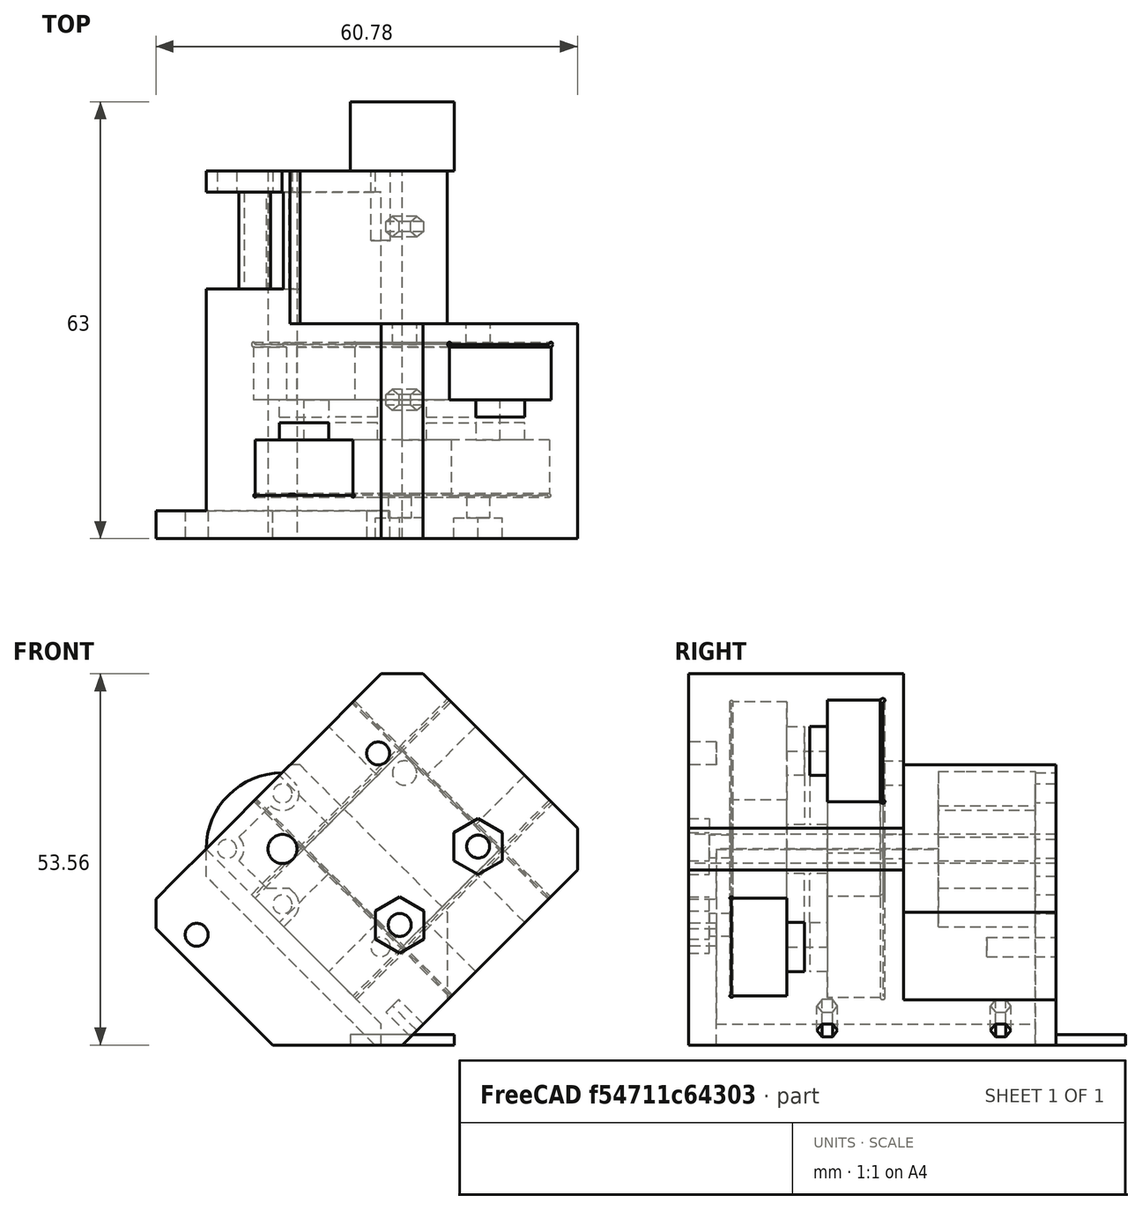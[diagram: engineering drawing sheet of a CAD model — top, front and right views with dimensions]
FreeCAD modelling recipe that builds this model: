
FCSTD DOCUMENT  (FreeCAD 0.19R)
Label: ToolHead_ScreenClearance
License: All rights reserved
LicenseURL: http://en.wikipedia.org/wiki/All_rights_reserved
objects: Sketcher::SketchObject×20, PartDesign::Pocket×14, PartDesign::Pad×4, PartDesign::Chamfer×2, PartDesign::Body×1, Mesh::Feature×1
note: 61 computed .brp shape members not serialized (recipe doc carries the construction recipe); baked Part::Feature solids carry a one-line shape summary decoded from their .brp

FEATURE [Sketcher::SketchObject] Sketch  label="Body001"
  FullyConstrained = true
  MapMode = 5
  Support = -> [XY_Plane]
  sketch-geometry (11):
    g0: LineSegment StartX=20 StartY=15.7574 StartZ=0 EndX=20 EndY=-15.7574 EndZ=0
    g1: LineSegment StartX=15.7574 StartY=-20 StartZ=0 EndX=-20 EndY=-20 EndZ=0
    g2: LineSegment StartX=-20 StartY=-15.7574 StartZ=0 EndX=-20 EndY=19.9515 EndZ=0
    g3: Circle CenterX=-12.1976 CenterY=12.1976 CenterZ=0 NormalX=0 NormalY=0 NormalZ=1 AngleXU=0 Radius=2.1
    g4: LineSegment StartX=-12.1976 StartY=12.1976 StartZ=0 EndX=0 EndY=0 EndZ=0
    g5: ArcOfCircle CenterX=-12.1976 CenterY=12.1976 CenterZ=0 NormalX=0 NormalY=0 NormalZ=1 AngleXU=0 Radius=11 StartAngle=0.788519 EndAngle=2.35931
    g6: LineSegment StartX=-4.44373 StartY=20 StartZ=0 EndX=15.7574 EndY=20 EndZ=0
    g7: LineSegment StartX=15.7574 StartY=-20 StartZ=0 EndX=20 EndY=-15.7574 EndZ=0
    g8: LineSegment StartX=-20 StartY=-15.7574 StartZ=0 EndX=-22.1213 EndY=-17.8787 EndZ=0
    g9: LineSegment StartX=-22.1213 StartY=-17.8787 StartZ=0 EndX=-20 EndY=-20 EndZ=0
    g10: LineSegment StartX=15.7574 StartY=20 StartZ=0 EndX=20 EndY=15.7574 EndZ=0
  constraints (32):
    c: Horizontal(g1)
    c: Vertical(g0)
    c: Vertical(g2)
    c: Distance(g-1,g3) = 17.25
    c: Coincident(g4,g3)
    c: Coincident(g4,g-1)
    c: Angle(g4) = -0.785398
    c: Diameter(g3) = 4.2
    c: Coincident(g5,g3)
    c: Diameter(g5) = 22
    c: DistanceX(g1) = -20
    c: Coincident(g6,g5)
    c: Horizontal(g6)
    c: Coincident(g5,g2)
    c: Coincident(g7,g1)
    c: Coincident(g7,g0)
    c: Angle(g7) = 0.785398
    c: Distance(g7) = 6
    c: DistanceY(g1) = -20
    c: Coincident(g2,g8)
    c: Coincident(g8,g9)
    c: Coincident(g9,g1)
    c: Angle(g9) = -0.785398
    c: Angle(g8) = -2.35619
    c: Distance(g9) = 3
    c: DistanceX(g2) = -20
    c: Coincident(g10,g6)
    c: Coincident(g10,g0)
    c: Distance(g10) = 6
    c: Angle(g10) = -0.785398
    c: DistanceX(g0) = 20
    c: DistanceY(g6) = 20
FEATURE [PartDesign::Pad] Pad
  Direction = (1,1,1)
  Length = 53
  Length2 = 10
  Profile = -> Sketch
  Reversed = true
  Type = 0
FEATURE [Sketcher::SketchObject] Sketch001  label="RailHole"
  FullyConstrained = true
  MapMode = 5
  Placement = pos=(20,0,0) rot=(0.57735,0.57735,0.57735;2.0944rad)
  Support = -> [Pad]
  sketch-geometry (10):
    g0: LineSegment StartX=-10.35 StartY=-27.65 StartZ=0 EndX=-10.35 EndY=-20 EndZ=0
    g1: LineSegment StartX=5 StartY=-17.5 StartZ=0 EndX=-5 EndY=-17.5 EndZ=0
    g2: LineSegment StartX=10 StartY=-28 StartZ=0 EndX=-10 EndY=-28 EndZ=0
    g3: LineSegment StartX=5 StartY=-17.5 StartZ=0 EndX=5 EndY=-20 EndZ=0
    g4: LineSegment StartX=-5 StartY=-20 StartZ=0 EndX=-5 EndY=-17.5 EndZ=0
    g5: LineSegment StartX=-10.35 StartY=-20 StartZ=0 EndX=-5 EndY=-20 EndZ=0
    g6: LineSegment StartX=5 StartY=-20 StartZ=0 EndX=10.3495 EndY=-20 EndZ=0
    g7: LineSegment StartX=10.3495 StartY=-27.65 StartZ=0 EndX=10.3495 EndY=-20 EndZ=0
    g8: ArcOfCircle CenterX=-10.35 CenterY=-28 CenterZ=0 NormalX=0 NormalY=0 NormalZ=1 AngleXU=0 Radius=0.35 StartAngle=1.5708 EndAngle=6.28319
    g9: ArcOfCircle CenterX=10.35 CenterY=-28 CenterZ=0 NormalX=0 NormalY=0 NormalZ=1 AngleXU=0 Radius=0.35 StartAngle=3.14159 EndAngle=7.85541
  constraints (29):
    c: Vertical(g0)
    c: Symmetric(g1,g1,g-2)
    c: Distance(g1) = 10
    c: Coincident(g1,g3)
    c: Vertical(g3)
    c: Coincident(g4,g1)
    c: Symmetric(g3,g4,g-2)
    c: Distance(g3) = 2.5
    c: Distance(g2) = 20
    c: Coincident(g5,g4)
    c: Horizontal(g5)
    c: Coincident(g3,g6)
    c: Horizontal(g6)
    c: Vertical(g7)
    c: Coincident(g0,g5)
    c: Coincident(g7,g6)
    c: Coincident(g0,g8)
    c: Coincident(g8,g2)
    c: Diameter(g8) = 0.7
    c: DistanceX(g0,g8) = 0
    c: DistanceY(g2,g8) = 0
    c: Coincident(g9,g2)
    c: Coincident(g9,g7)
    c: Diameter(g9) = 0.7
    c: DistanceY(g2,g9) = 0
    c: DistanceX(g7,g9) = 0.0005
    c: Symmetric(g9,g8,g-2)
    c: Distance(g9,g6) = 8
    c: DistanceY(g8) = -28
FEATURE [PartDesign::Pocket] Pocket
  BaseFeature = -> Pad
  Length = 5
  Length2 = 100
  Profile = -> Sketch001
  Type = 1
FEATURE [Sketcher::SketchObject] Sketch008  label="ExtruderHole"
  FullyConstrained = false
  MapMode = 5
  Placement = pos=(0,0,4) rot=(0,0,1;0rad)
  sketch-geometry (2):
    g0: LineSegment StartX=0 StartY=0 StartZ=0 EndX=-54.6242 EndY=54.6242 EndZ=0
    g1: Circle CenterX=-12.1976 CenterY=12.1976 CenterZ=0 NormalX=0 NormalY=0 NormalZ=1 AngleXU=0 Radius=2.1
  constraints (5):
    c: Coincident(g0,g-1)
    c: Angle(g0) = 2.35619
    c: PointOnObject(g1,g0)
    c: Distance(g-1,g1) = 17.25
    c: Diameter(g1) = 4.2
FEATURE [Sketcher::SketchObject] Sketch009  label="reference"
  FullyConstrained = false
  MapMode = 5
  Placement = pos=(0,0,-25) rot=(1,0,0;3.14159rad)
  sketch-geometry (2):
    g0: Circle CenterX=-12.0208 CenterY=-12.0208 CenterZ=0 NormalX=0 NormalY=0 NormalZ=1 AngleXU=0 Radius=10
    g1: LineSegment StartX=0 StartY=0 StartZ=0 EndX=-27.7674 EndY=-27.7674 EndZ=0
  constraints (5):
    c: Diameter(g0) = 20
    c: Coincident(g1,g-1)
    c: Angle(g1) = -2.35619
    c: PointOnObject(g0,g1)
    c: Distance(g0,g1) = 17
FEATURE [Sketcher::SketchObject] Sketch010  label="reference2"
  FullyConstrained = false
  MapMode = 5
  Placement = pos=(0,0,-37) rot=(1,0,0;3.14159rad)
  sketch-geometry (2):
    g0: Circle CenterX=-12.1976 CenterY=-12.1976 CenterZ=0 NormalX=0 NormalY=0 NormalZ=1 AngleXU=0 Radius=8
    g1: LineSegment StartX=0 StartY=0 StartZ=0 EndX=-38.1566 EndY=-38.1566 EndZ=0
  constraints (5):
    c: Diameter(g0) = 16
    c: Coincident(g1,g-1)
    c: Angle(g1) = -2.35619
    c: Distance(g0,g1) = 17.25
    c: PointOnObject(g0,g1)
FEATURE [Sketcher::SketchObject] Sketch021  label="InternalTri"
  FullyConstrained = true
  MapMode = 5
  Placement = pos=(0,-3e-15,-12) rot=(0,0,1;0rad)
  sketch-geometry (4):
    g0: LineSegment StartX=-10 StartY=10 StartZ=0 EndX=10 EndY=10 EndZ=0
    g1: LineSegment StartX=10 StartY=10 StartZ=0 EndX=10 EndY=-10 EndZ=0
    g2: LineSegment StartX=10 StartY=-10 StartZ=0 EndX=-10 EndY=-10 EndZ=0
    g3: LineSegment StartX=-10 StartY=-10 StartZ=0 EndX=-10 EndY=10 EndZ=0
  constraints (11):
    c: Coincident(g0,g1)
    c: Coincident(g1,g2)
    c: Coincident(g2,g3)
    c: Coincident(g3,g0)
    c: Horizontal(g0)
    c: Horizontal(g2)
    c: Vertical(g1)
    c: Vertical(g3)
    c: Symmetric(g1,g0,g-1)
    c: Equal(g1,g0)
    c: Distance(g1) = 20
FEATURE [PartDesign::Pocket] Pocket002
  BaseFeature = -> Pocket
  Length = 10
  Length2 = 2
  Profile = -> Sketch021
  Type = 4
FEATURE [Sketcher::SketchObject] Sketch019  label="RailHole2"
  FullyConstrained = true
  MapMode = 5
  Placement = pos=(0,-20,0) rot=(1,0,0;1.5708rad)
  Support = -> [Pocket002]
  sketch-geometry (10):
    g0: LineSegment StartX=-9.75 StartY=-6.2 StartZ=0 EndX=9.75 EndY=-6.2 EndZ=0
    g1: LineSegment StartX=10 StartY=-14.2 StartZ=0 EndX=5 EndY=-14.2 EndZ=0
    g2: LineSegment StartX=5 StartY=-14.2 StartZ=0 EndX=5 EndY=-16.7 EndZ=0
    g3: LineSegment StartX=5 StartY=-16.7 StartZ=0 EndX=-5 EndY=-16.7 EndZ=0
    g4: LineSegment StartX=-5 StartY=-16.7 StartZ=0 EndX=-5 EndY=-14.2 EndZ=0
    g5: LineSegment StartX=-5 StartY=-14.2 StartZ=0 EndX=-10 EndY=-14.2 EndZ=0
    g6: ArcOfCircle CenterX=10 CenterY=-6.2 CenterZ=0 NormalX=0 NormalY=0 NormalZ=1 AngleXU=0 Radius=0.25 StartAngle=4.71239 EndAngle=9.42478
    g7: ArcOfCircle CenterX=-10 CenterY=-6.2 CenterZ=0 NormalX=0 NormalY=0 NormalZ=1 AngleXU=0 Radius=0.25 StartAngle=-9e-16 EndAngle=4.71239
    g8: LineSegment StartX=-10 StartY=-14.2 StartZ=0 EndX=-10 EndY=-6.45 EndZ=0
    g9: LineSegment StartX=10 StartY=-14.2 StartZ=0 EndX=10 EndY=-6.45 EndZ=0
  constraints (29):
    c: Horizontal(g0)
    c: Horizontal(g1)
    c: Coincident(g1,g2)
    c: Vertical(g2)
    c: Coincident(g2,g3)
    c: Horizontal(g3)
    c: Coincident(g3,g4)
    c: Vertical(g4)
    c: Coincident(g4,g5)
    c: Symmetric(g1,g5,g-2)
    c: Distance(g3) = 10
    c: Symmetric(g4,g1,g-2)
    c: DistanceY(g0) = -6.2
    c: Distance(g2) = 2.5
    c: Coincident(g6,g0)
    c: Coincident(g7,g0)
    c: Distance(g7,g6) = 20
    c: DistanceY(g1,g6) = 8
    c: Coincident(g8,g5)
    c: Vertical(g8)
    c: Coincident(g9,g1)
    c: Coincident(g9,g6)
    c: Vertical(g9)
    c: Coincident(g7,g8)
    c: Symmetric(g6,g7,g-2)
    c: Diameter(g6) = 0.5
    c: Equal(g6,g7)
    c: DistanceX(g7,g7) = 0
    c: DistanceY(g7,g0) = 0
FEATURE [Sketcher::SketchObject] Sketch024  label="hgxLITEholes"
  FullyConstrained = false
  MapMode = 5
  Placement = pos=(0,0,4) rot=(0,0,1;0rad)
  sketch-geometry (5):
    g0: Circle CenterX=7.30241 CenterY=12.1976 CenterZ=0 NormalX=0 NormalY=0 NormalZ=1 AngleXU=0 Radius=1.65
    g1: Circle CenterX=-29.6976 CenterY=12.1976 CenterZ=0 NormalX=0 NormalY=0 NormalZ=1 AngleXU=0 Radius=1.65
    g2: LineSegment StartX=-29.6976 StartY=12.1976 StartZ=0 EndX=7.30241 EndY=12.1976 EndZ=0
    g3: LineSegment StartX=0 StartY=0 StartZ=0 EndX=-27.1729 EndY=27.1729 EndZ=0
    g4: Circle CenterX=-12.1976 CenterY=12.1976 CenterZ=0 NormalX=0 NormalY=0 NormalZ=1 AngleXU=0 Radius=1.0154
  constraints (12):
    c: Diameter(g0) = 3.3
    c: Equal(g0,g1)
    c: Coincident(g2,g1)
    c: Coincident(g2,g0)
    c: Distance(g2) = 37
    c: Coincident(g3,g-1)
    c: Angle(g3) = 2.35619
    c: PointOnObject(g4,g3)
    c: Distance(g-1,g4) = 17.25
    c: Distance(g4,g0) = 19.5
    c: Horizontal(g2)
    c: PointOnObject(g4,g2)
FEATURE [PartDesign::Pocket] Pocket003
  BaseFeature = -> Pocket002
  Length = 5
  Length2 = 100
  Profile = -> Sketch019
  Type = 1
FEATURE [Sketcher::SketchObject] Sketch026  label="BottomSculp"
  FullyConstrained = false
  MapMode = 5
  Placement = pos=(0,0,-53) rot=(1,0,0;3.14159rad)
  Support = -> [Pocket003]
  sketch-geometry (5):
    g0: LineSegment StartX=29.4648 StartY=27.8981 StartZ=0 EndX=28.2209 EndY=-23.4245 EndZ=0
    g1: LineSegment StartX=28.2209 StartY=-23.4245 StartZ=0 EndX=-1.84855 EndY=-23.4245 EndZ=0
    g2: LineSegment StartX=-1.84855 StartY=-23.4245 StartZ=0 EndX=-1.84854 EndY=11.0762 EndZ=0
    g3: LineSegment StartX=-1.84854 StartY=11.0762 StartZ=0 EndX=-16.3575 EndY=25.5852 EndZ=0
    g4: LineSegment StartX=-16.3575 StartY=25.5852 StartZ=0 EndX=29.4648 EndY=27.8981 EndZ=0
  constraints (8):
    c: Coincident(g0,g1)
    c: Horizontal(g1)
    c: Coincident(g1,g2)
    c: Angle(g2) = 1.5708
    c: Coincident(g2,g3)
    c: Angle(g3) = 2.35619
    c: Coincident(g4,g3)
    c: Coincident(g4,g0)
FEATURE [PartDesign::Pocket] Pocket004
  BaseFeature = -> Pocket003
  Length = 22
  Length2 = 100
  Profile = -> Sketch026
  Type = 0
FEATURE [Sketcher::SketchObject] Sketch004  label="Yboltpattern"
  FullyConstrained = true
  MapMode = 5
  Placement = pos=(0,0,-31) rot=(1,0,0;3.14159rad)
  Support = -> [Pocket004]
  sketch-geometry (8):
    g0: Circle CenterX=-8 CenterY=7.5 CenterZ=0 NormalX=0 NormalY=0 NormalZ=1 AngleXU=0 Radius=1.75
    g1: Circle CenterX=8 CenterY=7.5 CenterZ=0 NormalX=0 NormalY=0 NormalZ=1 AngleXU=0 Radius=1.75
    g2: Circle CenterX=-8 CenterY=-7.5 CenterZ=0 NormalX=0 NormalY=0 NormalZ=1 AngleXU=0 Radius=1.75
    g3: Circle CenterX=8 CenterY=-7.5 CenterZ=0 NormalX=0 NormalY=0 NormalZ=1 AngleXU=0 Radius=1.75
    g4: LineSegment StartX=-8 StartY=7.5 StartZ=0 EndX=8 EndY=7.5 EndZ=0
    g5: LineSegment StartX=8 StartY=7.5 StartZ=0 EndX=8 EndY=-7.5 EndZ=0
    g6: LineSegment StartX=8 StartY=-7.5 StartZ=0 EndX=-8 EndY=-7.5 EndZ=0
    g7: LineSegment StartX=-8 StartY=-7.5 StartZ=0 EndX=-8 EndY=7.5 EndZ=0
  constraints (18):
    c: Diameter(g0) = 3.5
    c: Equal(g0,g1)
    c: Equal(g0,g2)
    c: Equal(g0,g3)
    c: Distance(g2,g0) = 15
    c: Distance(g3,g2) = 16
    c: Coincident(g4,g0)
    c: Coincident(g4,g1)
    c: Coincident(g4,g5)
    c: Coincident(g5,g3)
    c: Coincident(g5,g6)
    c: Coincident(g6,g2)
    c: Coincident(g6,g7)
    c: Coincident(g7,g4)
    c: Equal(g5,g7)
    c: Equal(g4,g6)
    c: Symmetric(g1,g2,g-1)
    c: Symmetric(g0,g1,g-2)
FEATURE [Sketcher::SketchObject] Sketch022  label="VoronHoleRelif"
  FullyConstrained = true
  MapMode = 5
  Placement = pos=(0,0,-28) rot=(0,0,1;0rad)
  Support = -> [Pocket004]
  sketch-geometry (11):
    g0: ArcOfCircle CenterX=-17.8884 CenterY=6.52425 CenterZ=0 NormalX=0 NormalY=0 NormalZ=1 AngleXU=0 Radius=2.4 StartAngle=4.71239 EndAngle=6.28319
    g1: ArcOfCircle CenterX=-6.58192 CenterY=17.8307 CenterZ=0 NormalX=0 NormalY=0 NormalZ=1 AngleXU=0 Radius=2.4 StartAngle=3.14159 EndAngle=6.28319
    g2: LineSegment StartX=-22.2684 StartY=4.12425 StartZ=0 EndX=-17.8884 EndY=4.12425 EndZ=0
    g3: LineSegment StartX=-22.2684 StartY=23.8307 StartZ=0 EndX=-4.18192 EndY=23.8307 EndZ=0
    g4: LineSegment StartX=-4.18192 StartY=23.8307 StartZ=0 EndX=-4.18192 EndY=17.8307 EndZ=0
    g5: LineSegment StartX=-22.2684 StartY=4.12425 StartZ=0 EndX=-22.2684 EndY=23.8307 EndZ=0
    g6: ArcOfCircle CenterX=-17.8172 CenterY=17.8307 CenterZ=0 NormalX=0 NormalY=0 NormalZ=1 AngleXU=0 Radius=2.4 StartAngle=4.71239 EndAngle=6.28319
    g7: LineSegment StartX=-15.4172 StartY=17.8307 StartZ=0 EndX=-8.98192 EndY=17.8307 EndZ=0
    g8: LineSegment StartX=-17.8172 StartY=9.85307 StartZ=0 EndX=-15.4884 EndY=7.52425 EndZ=0
    g9: LineSegment StartX=-15.4884 StartY=6.52425 StartZ=0 EndX=-15.4884 EndY=7.52425 EndZ=0
    g10: LineSegment StartX=-17.8172 StartY=9.85307 StartZ=0 EndX=-17.8172 EndY=15.4307 EndZ=0
  constraints (33):
    c: Horizontal(g2)
    c: Coincident(g3,g4)
    c: Tangent(g4,g1) = 1.5708
    c: Tangent(g2,g0) = -1.5708
    c: Diameter(g0) = 4.8
    c: Equal(g0,g1)
    c: Vertical(g4)
    c: Horizontal(g3)
    c: Coincident(g5,g2)
    c: Coincident(g5,g3)
    c: Vertical(g5)
    c: Distance(g2) = 4.38
    c: Distance(g4) = 6
    c: DistanceX(g1) = -6.58192
    c: DistanceY(g1) = 17.8307
    c: DistanceX(g0) = -17.8884
    c: DistanceY(g0) = 6.52425
    c: Coincident(g7,g6)
    c: Coincident(g7,g1)
    c: Horizontal(g7)
    c: Perpendicular(g1,g7)
    c: Diameter(g6) = 4.8
    c: Perpendicular(g6,g7)
    c: Angle(g8) = -0.785398
    c: Vertical(g9)
    c: Tangent(g9,g0) = -1.5708
    c: Distance(g9) = 1
    c: Coincident(g8,g9)
    c: Coincident(g10,g8)
    c: Coincident(g10,g6)
    c: Vertical(g10)
    c: Perpendicular(g6,g10)
    c: DistanceX(g6) = -17.8172
FEATURE [PartDesign::Pocket] Pocket005
  BaseFeature = -> Pocket004
  Length = 22
  Length2 = -8
  Profile = -> Sketch022
  Type = 4
FEATURE [Sketcher::SketchObject] Sketch017  label="VoronHoles3"
  FullyConstrained = true
  MapMode = 5
  Placement = pos=(0,0,-50) rot=(0,0,1;0rad)
  Support = -> [Pocket005]
  sketch-geometry (10):
    g0: Circle CenterX=-6.54074 CenterY=17.8544 CenterZ=0 NormalX=0 NormalY=0 NormalZ=1 AngleXU=0 Radius=1.375
    g1: Circle CenterX=-17.8544 CenterY=6.54074 CenterZ=0 NormalX=0 NormalY=0 NormalZ=1 AngleXU=0 Radius=1.375
    g2: Circle CenterX=-6.54074 CenterY=6.54074 CenterZ=0 NormalX=0 NormalY=0 NormalZ=1 AngleXU=0 Radius=1.375
    g3: Circle CenterX=-17.8544 CenterY=17.8544 CenterZ=0 NormalX=0 NormalY=0 NormalZ=1 AngleXU=0 Radius=1.375
    g4: LineSegment StartX=-6.54074 StartY=17.8544 StartZ=0 EndX=-6.54074 EndY=6.54074 EndZ=0
    g5: LineSegment StartX=-6.54074 StartY=6.54074 StartZ=0 EndX=-17.8544 EndY=6.54074 EndZ=0
    g6: LineSegment StartX=-17.8544 StartY=6.54074 StartZ=0 EndX=-17.8544 EndY=17.8544 EndZ=0
    g7: LineSegment StartX=-17.8544 StartY=17.8544 StartZ=0 EndX=-6.54074 EndY=17.8544 EndZ=0
    g8: LineSegment StartX=0 StartY=0 StartZ=0 EndX=-37.1726 EndY=37.1726 EndZ=0
    g9: Circle CenterX=-12.1976 CenterY=12.1976 CenterZ=0 NormalX=0 NormalY=0 NormalZ=1 AngleXU=0 Radius=0.77
  constraints (25):
    c: Coincident(g4,g0)
    c: Coincident(g4,g2)
    c: Coincident(g4,g5)
    c: Coincident(g5,g1)
    c: Coincident(g5,g6)
    c: Coincident(g6,g3)
    c: Coincident(g6,g7)
    c: Coincident(g7,g4)
    c: Equal(g4,g7)
    c: Equal(g7,g6)
    c: Equal(g6,g5)
    c: Coincident(g8,g-1)
    c: PointOnObject(g9,g8)
    c: Distance(g-1,g9) = 17.25
    c: Diameter(g1) = 2.75
    c: Equal(g1,g3)
    c: Equal(g1,g0)
    c: Equal(g1,g2)
    c: Symmetric(g0,g1,g9)
    c: Distance(g2,g3) = 16
    c: Angle(g8) = 2.35619
    c: PointOnObject(g2,g8)
    c: Perpendicular(g7,g4)
    c: Distance(g8) = 52.57
    c: Diameter(g9) = 1.54
FEATURE [PartDesign::Pocket] Pocket006
  BaseFeature = -> Pocket005
  Length = 5
  Length2 = 100
  Profile = -> Sketch017
  Type = 1
FEATURE [Sketcher::SketchObject] Sketch025  label="FanDuctMountHole"
  FullyConstrained = true
  MapMode = 5
  Placement = pos=(0,0,-53) rot=(1,0,0;3.14159rad)
  Support = -> [Pocket006]
  sketch-geometry (1):
    g0: Circle CenterX=-12.2 CenterY=7.8 CenterZ=0 NormalX=0 NormalY=0 NormalZ=1 AngleXU=0 Radius=1.4
  constraints (3):
    c: Diameter(g0) = 2.8
    c: DistanceX(g0) = -12.2
    c: DistanceY(g0) = 7.8
FEATURE [PartDesign::Pocket] Pocket007
  BaseFeature = -> Pocket006
  Length = 10
  Length2 = 100
  Profile = -> Sketch025
  Type = 0
FEATURE [PartDesign::Pocket] Pocket008
  BaseFeature = -> Pocket007
  Length = 9
  Length2 = 100
  Profile = -> Sketch004
  Type = 0
FEATURE [Sketcher::SketchObject] Sketch007  label="ExtruderPlatform"
  ExternalGeometry = -> [Pad]
  FullyConstrained = false
  MapMode = 5
  Support = -> [Pocket008]
  sketch-geometry (12):
    g0: LineSegment StartX=-20 StartY=-20 StartZ=0 EndX=15.7574 EndY=-20 EndZ=0
    g1: LineSegment StartX=0 StartY=0 StartZ=0 EndX=-70.7107 EndY=70.7107 EndZ=0
    g2: Circle CenterX=-12.1976 CenterY=12.1976 CenterZ=0 NormalX=0 NormalY=0 NormalZ=1 AngleXU=0 Radius=2.125
    g3: LineSegment StartX=15.7574 StartY=-20 StartZ=0 EndX=20 EndY=-15.7574 EndZ=0
    g4: LineSegment StartX=20 StartY=-15.7574 StartZ=0 EndX=20 EndY=15.7574 EndZ=0
    g5: LineSegment StartX=20 StartY=15.7574 StartZ=0 EndX=15.7574 EndY=20 EndZ=0
    g6: LineSegment StartX=-20 StartY=-20 StartZ=0 EndX=-33.1976 EndY=-6.80241 EndZ=0
    g7: LineSegment StartX=-12.1976 StartY=-100 StartZ=0 EndX=-12.1976 EndY=100 EndZ=0
    g8: LineSegment StartX=-33.1976 StartY=-6.80241 StartZ=0 EndX=-33.1976 EndY=20 EndZ=0
    g9: LineSegment StartX=-33.1976 StartY=20 StartZ=0 EndX=15.7574 EndY=20 EndZ=0
    g10: Circle CenterX=-29.6976 CenterY=12.1976 CenterZ=0 NormalX=0 NormalY=0 NormalZ=1 AngleXU=0 Radius=1.4
    g11: Circle CenterX=7.30241 CenterY=11.9057 CenterZ=0 NormalX=0 NormalY=0 NormalZ=1 AngleXU=0 Radius=1.4
  constraints (35):
    c: Coincident(g1,g-1)
    c: Angle(g1) = 2.35619
    c: Diameter(g2) = 4.25
    c: PointOnObject(g2,g1)
    c: Distance(g-1,g2) = 17.25
    c: Coincident(g0,g3)
    c: Coincident(g3,g4)
    c: Coincident(g6,g0)
    c: Angle(g6) = 2.35619
    c: Coincident(g5,g4)
    c: Distance(g1) = 100
    c: PointOnObject(g2,g7)
    c: DistanceX(g0,g0) = -35.7574
    c: DistanceY(g0,g0) = 0
    c: DistanceX(g3,g0) = -40
    c: DistanceY(g3,g0) = -4.24264
    c: DistanceX(g4) = 20
    c: DistanceY(g4) = 15.7574
    c: DistanceX(g3) = 20
    c: DistanceY(g3) = -15.7574
    c: Coincident(g8,g6)
    c: Vertical(g8)
    c: Horizontal(g9)
    c: Coincident(g5,g9)
    c: Distance(g8,g7) = 21
    c: DistanceX(g5) = 15.7574
    c: DistanceY(g5) = 20
    c: Symmetric(g7,g7,g-1)
    c: Distance(g7) = 200
    c: DistanceX(g10,g2) = 17.5
    c: DistanceX(g2,g11) = 19.5
    c: Diameter(g10) = 2.8
    c: Equal(g10,g11)
    c: DistanceY(g10,g2) = 0
    c: Coincident(g9,g8)
FEATURE [PartDesign::Pad] Pad001
  BaseFeature = -> Pocket008
  Direction = (1,1,1)
  Length = 4
  Length2 = 100
  Profile = -> Sketch007
  Reversed = true
  Type = 0
FEATURE [PartDesign::Pocket] Pocket009
  BaseFeature = -> Pad001
  Length = 8
  Length2 = 100
  Profile = -> Sketch024
  Type = 0
FEATURE [PartDesign::Pocket] Pocket010
  BaseFeature = -> Pocket009
  Length = 5
  Length2 = 100
  Profile = -> Sketch008
  Type = 1
FEATURE [Sketcher::SketchObject] Sketch003  label="Xboltpattern"
  FullyConstrained = true
  MapMode = 5
  Support = -> [Pocket010]
  sketch-geometry (8):
    g0: Circle CenterX=-8 CenterY=7.5 CenterZ=0 NormalX=0 NormalY=0 NormalZ=1 AngleXU=0 Radius=1.65
    g1: Circle CenterX=8 CenterY=7.5 CenterZ=0 NormalX=0 NormalY=0 NormalZ=1 AngleXU=0 Radius=1.65
    g2: Circle CenterX=-8 CenterY=-7.5 CenterZ=0 NormalX=0 NormalY=0 NormalZ=1 AngleXU=0 Radius=1.65
    g3: Circle CenterX=8 CenterY=-7.5 CenterZ=0 NormalX=0 NormalY=0 NormalZ=1 AngleXU=0 Radius=1.65
    g4: LineSegment StartX=-8 StartY=7.5 StartZ=0 EndX=8 EndY=7.5 EndZ=0
    g5: LineSegment StartX=8 StartY=7.5 StartZ=0 EndX=8 EndY=-7.5 EndZ=0
    g6: LineSegment StartX=8 StartY=-7.5 StartZ=0 EndX=-8 EndY=-7.5 EndZ=0
    g7: LineSegment StartX=-8 StartY=-7.5 StartZ=0 EndX=-8 EndY=7.5 EndZ=0
  constraints (19):
    c: Diameter(g0) = 3.3
    c: Equal(g0,g1)
    c: Equal(g0,g2)
    c: Equal(g0,g3)
    c: Distance(g0,g1) = 16
    c: Distance(g1,g3) = 15
    c: Coincident(g4,g0)
    c: Coincident(g4,g1)
    c: Horizontal(g4)
    c: Coincident(g4,g5)
    c: Coincident(g5,g3)
    c: Vertical(g5)
    c: Coincident(g5,g6)
    c: Coincident(g6,g2)
    c: Coincident(g6,g7)
    c: Coincident(g7,g4)
    c: Symmetric(g2,g1,g-1)
    c: Equal(g7,g5)
    c: Equal(g6,g4)
FEATURE [Sketcher::SketchObject] Sketch029  label="Adhesion"
  FullyConstrained = false
  MapMode = 5
  Placement = pos=(0,0,-53) rot=(1,0,0;3.14159rad)
  sketch-geometry (4):
    g0: LineSegment StartX=-13.636 StartY=24.2426 StartZ=0 EndX=-24.2426 EndY=13.636 EndZ=0
    g1: LineSegment StartX=-24.2426 StartY=13.636 StartZ=0 EndX=-25.3033 EndY=14.6967 EndZ=0
    g2: LineSegment StartX=-25.3033 StartY=14.6967 StartZ=0 EndX=-14.6967 EndY=25.3033 EndZ=0
    g3: LineSegment StartX=-14.6967 StartY=25.3033 StartZ=0 EndX=-13.636 EndY=24.2426 EndZ=0
  constraints (10):
    c: Coincident(g0,g1)
    c: Coincident(g1,g2)
    c: Coincident(g2,g3)
    c: Coincident(g3,g0)
    c: Angle(g2) = 0.785398
    c: Distance(g2) = 15
    c: Distance(g1) = 1.5
    c: Distance(g3) = 1.5
    c: Perpendicular(g2,g3)
    c: Perpendicular(g2,g1)
FEATURE [Sketcher::SketchObject] Sketch033  label="WireMgmnt"
  FullyConstrained = true
  MapMode = 5
  Placement = pos=(0,-20,0) rot=(1,0,0;1.5708rad)
  sketch-geometry (14):
    g0: LineSegment StartX=-15.7 StartY=-20.7506 StartZ=0 EndX=-15.7 EndY=-19.2494 EndZ=0
    g1: LineSegment StartX=-15.7 StartY=-19.2494 StartZ=0 EndX=-17 EndY=-18.4989 EndZ=0
    g2: LineSegment StartX=-17 StartY=-18.4989 StartZ=0 EndX=-18.3 EndY=-19.2494 EndZ=0
    g3: LineSegment StartX=-18.3 StartY=-19.2494 StartZ=0 EndX=-18.3 EndY=-20.7506 EndZ=0
    g4: LineSegment StartX=-18.3 StartY=-20.7506 StartZ=0 EndX=-17 EndY=-21.5011 EndZ=0
    g5: LineSegment StartX=-17 StartY=-21.5011 StartZ=0 EndX=-15.7 EndY=-20.7506 EndZ=0
    g6: Circle CenterX=-17 CenterY=-20 CenterZ=0 NormalX=0 NormalY=0 NormalZ=1 AngleXU=0 Radius=1.50111
    g7: LineSegment StartX=-15.7 StartY=-44.2494 StartZ=0 EndX=-17 EndY=-43.4989 EndZ=0
    g8: LineSegment StartX=-17 StartY=-43.4989 StartZ=0 EndX=-18.3 EndY=-44.2494 EndZ=0
    g9: LineSegment StartX=-18.3 StartY=-44.2494 StartZ=0 EndX=-18.3 EndY=-45.7506 EndZ=0
    g10: LineSegment StartX=-18.3 StartY=-45.7506 StartZ=0 EndX=-17 EndY=-46.5011 EndZ=0
    g11: LineSegment StartX=-17 StartY=-46.5011 StartZ=0 EndX=-15.7 EndY=-45.7506 EndZ=0
    g12: LineSegment StartX=-15.7 StartY=-45.7506 StartZ=0 EndX=-15.7 EndY=-44.2494 EndZ=0
    g13: Circle CenterX=-17 CenterY=-45 CenterZ=0 NormalX=0 NormalY=0 NormalZ=1 AngleXU=0 Radius=1.50111
  constraints (34):
    c: Coincident(g0,g1)
    c: Coincident(g1,g2)
    c: Coincident(g2,g3)
    c: Coincident(g3,g4)
    c: Coincident(g4,g5)
    c: Coincident(g5,g0)
    c: Equal(g0, g1-g5) x5
    c: PointOnObject(g0,g6)
    c: PointOnObject(g1,g6)
    c: PointOnObject(g2,g6)
    c: PointOnObject(g3,g6)
    c: PointOnObject(g4,g6)
    c: PointOnObject(g5,g6)
    c: Coincident(g7,g8)
    c: Coincident(g8,g9)
    c: Coincident(g9,g10)
    c: Coincident(g10,g11)
    c: Coincident(g11,g12)
    c: Coincident(g12,g7)
    c: Equal(g7, g8-g12) x5
    c: PointOnObject(g7,g13)
    c: PointOnObject(g8,g13)
    c: PointOnObject(g9,g13)
    c: PointOnObject(g10,g13)
    c: PointOnObject(g11,g13)
    c: PointOnObject(g12,g13)
    c: DistanceX(g13) = -17
    c: Distance(g10,g7) = 2.6
    c: Vertical(g9)
    c: DistanceY(g13) = -45
    c: Distance(g3,g0) = 2.6
    c: DistanceY(g6) = -20
    c: Vertical(g3)
    c: DistanceX(g6) = -17
FEATURE [Sketcher::SketchObject] Sketch035  label="Bottom Reinforce"
  FullyConstrained = false
  MapMode = 5
  Placement = pos=(0,0,-53) rot=(1,0,0;3.14159rad)
  sketch-geometry (4):
    g0: LineSegment StartX=-22.779 StartY=17.221 StartZ=0 EndX=-22.779 EndY=-17.1725 EndZ=0
    g1: LineSegment StartX=-22.779 StartY=-17.1725 StartZ=0 EndX=-20 EndY=-19.9515 EndZ=0
    g2: LineSegment StartX=-20 StartY=-19.9515 StartZ=0 EndX=-20 EndY=20 EndZ=0
    g3: LineSegment StartX=-20 StartY=20 StartZ=0 EndX=-22.779 EndY=17.221 EndZ=0
  constraints (9):
    c: Vertical(g0)
    c: Coincident(g0,g1)
    c: Coincident(g1,g2)
    c: Vertical(g2)
    c: Coincident(g2,g3)
    c: Coincident(g3,g0)
    c: Angle(g1) = -0.785398
    c: DistanceY(g2) = 20
    c: Angle(g3) = -2.35619
FEATURE [Sketcher::SketchObject] Sketch037
  FullyConstrained = false
  MapMode = 5
  sketch-geometry (4):
    g0: LineSegment StartX=-26.2848 StartY=31.2083 StartZ=0 EndX=-1.26106 EndY=31.2083 EndZ=0
    g1: LineSegment StartX=-1.26106 StartY=31.2083 StartZ=0 EndX=-1.26106 EndY=20 EndZ=0
    g2: LineSegment StartX=-1.26106 StartY=20 StartZ=0 EndX=-26.2848 EndY=20 EndZ=0
    g3: LineSegment StartX=-26.2848 StartY=20 StartZ=0 EndX=-26.2848 EndY=31.2083 EndZ=0
  constraints (9):
    c: Coincident(g0,g1)
    c: Coincident(g1,g2)
    c: Coincident(g2,g3)
    c: Coincident(g3,g0)
    c: Horizontal(g0)
    c: Horizontal(g2)
    c: Vertical(g1)
    c: Vertical(g3)
    c: DistanceY(g1) = 20
FEATURE [PartDesign::Pocket] Pocket011
  BaseFeature = -> Pocket010
  Length = 10
  Length2 = 100
  Profile = -> Sketch003
  Type = 0
FEATURE [Sketcher::SketchObject] Sketch036  label="countersink"
  FullyConstrained = true
  MapMode = 5
  Support = -> [Pocket011]
  sketch-geometry (14):
    g0: LineSegment StartX=11.9037 StartY=-8.546 StartZ=0 EndX=10.8577 EndY=-4.64226 EndZ=0
    g1: LineSegment StartX=10.8577 StartY=-4.64226 StartZ=0 EndX=6.954 EndY=-3.59626 EndZ=0
    g2: LineSegment StartX=6.954 StartY=-3.59626 StartZ=0 EndX=4.09626 EndY=-6.454 EndZ=0
    g3: LineSegment StartX=4.09626 StartY=-6.454 StartZ=0 EndX=5.14226 EndY=-10.3577 EndZ=0
    g4: LineSegment StartX=5.14226 StartY=-10.3577 StartZ=0 EndX=9.046 EndY=-11.4037 EndZ=0
    g5: LineSegment StartX=9.046 StartY=-11.4037 StartZ=0 EndX=11.9037 EndY=-8.546 EndZ=0
    g6: Circle CenterX=8 CenterY=-7.5 CenterZ=0 NormalX=0 NormalY=0 NormalZ=1 AngleXU=0 Radius=4.04145
    g7: LineSegment StartX=-5.14226 StartY=-4.64226 StartZ=0 EndX=-9.046 EndY=-3.59626 EndZ=0
    g8: LineSegment StartX=-9.046 StartY=-3.59626 StartZ=0 EndX=-11.9037 EndY=-6.454 EndZ=0
    g9: LineSegment StartX=-11.9037 StartY=-6.454 StartZ=0 EndX=-10.8577 EndY=-10.3577 EndZ=0
    g10: LineSegment StartX=-10.8577 StartY=-10.3577 StartZ=0 EndX=-6.954 EndY=-11.4037 EndZ=0
    g11: LineSegment StartX=-6.954 StartY=-11.4037 StartZ=0 EndX=-4.09626 EndY=-8.546 EndZ=0
    g12: LineSegment StartX=-4.09626 StartY=-8.546 StartZ=0 EndX=-5.14226 EndY=-4.64226 EndZ=0
    g13: Circle CenterX=-8 CenterY=-7.5 CenterZ=0 NormalX=0 NormalY=0 NormalZ=1 AngleXU=0 Radius=4.04145
  constraints (34):
    c: Coincident(g0,g1)
    c: Coincident(g1,g2)
    c: Coincident(g2,g3)
    c: Coincident(g3,g4)
    c: Coincident(g4,g5)
    c: Coincident(g5,g0)
    c: Equal(g0, g1-g5) x5
    c: PointOnObject(g0,g6)
    c: PointOnObject(g1,g6)
    c: PointOnObject(g2,g6)
    c: PointOnObject(g3,g6)
    c: PointOnObject(g4,g6)
    c: PointOnObject(g5,g6)
    c: Coincident(g7,g8)
    c: Coincident(g8,g9)
    c: Coincident(g9,g10)
    c: Coincident(g10,g11)
    c: Coincident(g11,g12)
    c: Coincident(g12,g7)
    c: Equal(g7, g8-g12) x5
    c: PointOnObject(g7,g13)
    c: PointOnObject(g8,g13)
    c: PointOnObject(g9,g13)
    c: PointOnObject(g10,g13)
    c: PointOnObject(g11,g13)
    c: PointOnObject(g12,g13)
    c: Angle(g11) = 0.785398
    c: Angle(g5) = 0.785398
    c: Distance(g0,g2) = 7
    c: Distance(g7,g8) = 7
    c: DistanceX(g6) = 8
    c: DistanceY(g6) = -7.5
    c: DistanceY(g13) = -7.5
    c: DistanceX(g13) = -8
FEATURE [PartDesign::Pocket] Pocket012
  BaseFeature = -> Pocket011
  Length = 3
  Length2 = 100
  Profile = -> Sketch036
  Type = 0
FEATURE [PartDesign::Pocket] Pocket013
  BaseFeature = -> Pocket012
  Length = 5
  Length2 = 100
  Profile = -> Sketch033
  Type = 0
FEATURE [PartDesign::Pad] Pad002
  BaseFeature = -> Pocket013
  Direction = (1,1,1)
  Length = 3
  Length2 = 100
  Profile = -> Sketch035
  Reversed = true
  Type = 0
FEATURE [PartDesign::Pocket] Pocket014
  BaseFeature = -> Pad002
  Length = 40
  Length2 = 100
  Profile = -> Sketch037
  Type = 0
FEATURE [PartDesign::Pad] Pad003
  BaseFeature = -> Pocket014
  Direction = (1,1,1)
  Length = 10
  Length2 = 100
  Profile = -> Sketch029
  Type = 0
FEATURE [PartDesign::Chamfer] Chamfer
  Angle = 45
  Base = -> Pad003 [Edge248]
  BaseFeature = -> Pad003
  ChamferType = 0
  FlipDirection = false
  Size = 1
  Size2 = 1
  SupportTransform = false
FEATURE [PartDesign::Chamfer] Chamfer001
  Angle = 45
  Base = -> Chamfer [Edge357]
  BaseFeature = -> Chamfer
  ChamferType = 0
  FlipDirection = false
  Size = 3
  Size2 = 1
  SupportTransform = false
FEATURE [PartDesign::Body] Body
  Group = -> [Sketch,Pad,Sketch001,Pocket,Sketch003,Sketch004,Sketch007,Sketch008,Sketch009,Sketch010,Sketch017,Sketch019,Sketch021,Pocket002,Sketch022,Sketch024,Sketch025,Sketch026,Pocket003,Pocket004,Pocket005,Pocket006,Pocket007,Pocket008,Pad001,Pocket009,Pocket010,Sketch029,Sketch033,Sketch035,Sketch036,Sketch037,Pocket011,Pocket012,Pocket013,Pad002,Pocket014,Pad003,Chamfer,Chamfer001]
  Origin = -> Origin
  Placement = pos=(0,0,0) rot=(0.862856,-0.357407,0.357407;1.71777rad)
  Tip = -> Chamfer001
FEATURE [Mesh::Feature] Mesh  label="Chamfer001 (Meshed)"
